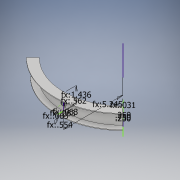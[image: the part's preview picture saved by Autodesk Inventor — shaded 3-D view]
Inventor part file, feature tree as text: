
AUTODESK INVENTOR PART (.ipt)
format: ipt  version: 2017 (Build 210142000, 142)  size: 168,960 bytes
history: native  units: in
note: dims shown in document units (in); Inventor stores cm internally (conversion verified against a paired STEP export)
features: sketch x5, extrude x4, revolve x1, plane x1
ambient origin geometry x8: Origin, YZ Plane, XZ Plane, XY Plane, X Axis, Y Axis, Z Axis, Center Point
bodies: Solid1 (feature_tree)
feature tree (11):
  revolve  "Revolution1"  [1 undecoded]
  plane  "Work Plane1"
  sketch  "Sketch2"  dims[d3=1.4364in d4=0.0625in]
  extrude  "Extrusion2"  Depth=0.0625in
  extrude  "Extrusion3"  TaperAngle=90.0deg  [1 undecoded]
  extrude  "Extrusion4"  Depth=0.375in
  extrude  "Extrusion5"  Depth=0.0312in TaperAngle=0.0deg
  sketch  "Sketch5"  dims[d11=0.3125in d12=1.0in d13=0.0in d14=0.0156in d15=0.0in d16=0.25in d17=0.0625in d18=0.0in d19=135.0deg d20=0.0in d21=0.0in d22=0.75in d23=0.0312in d24=0.25in d25=0.25in]
  sketch  "Sketch1"  dims[d1=0.5536in d2=0.0625in]
  sketch  "Sketch3"  dims[d5=0.0625in d6=90.0deg]
  sketch  "Sketch4"  dims[d7=0.562in d8=0.375in]
note: 2 required parameter values undecoded (feature->parameter linkage not recoverable at this tier; creation-order binding heuristic only, values carry confidence <= 0.55)